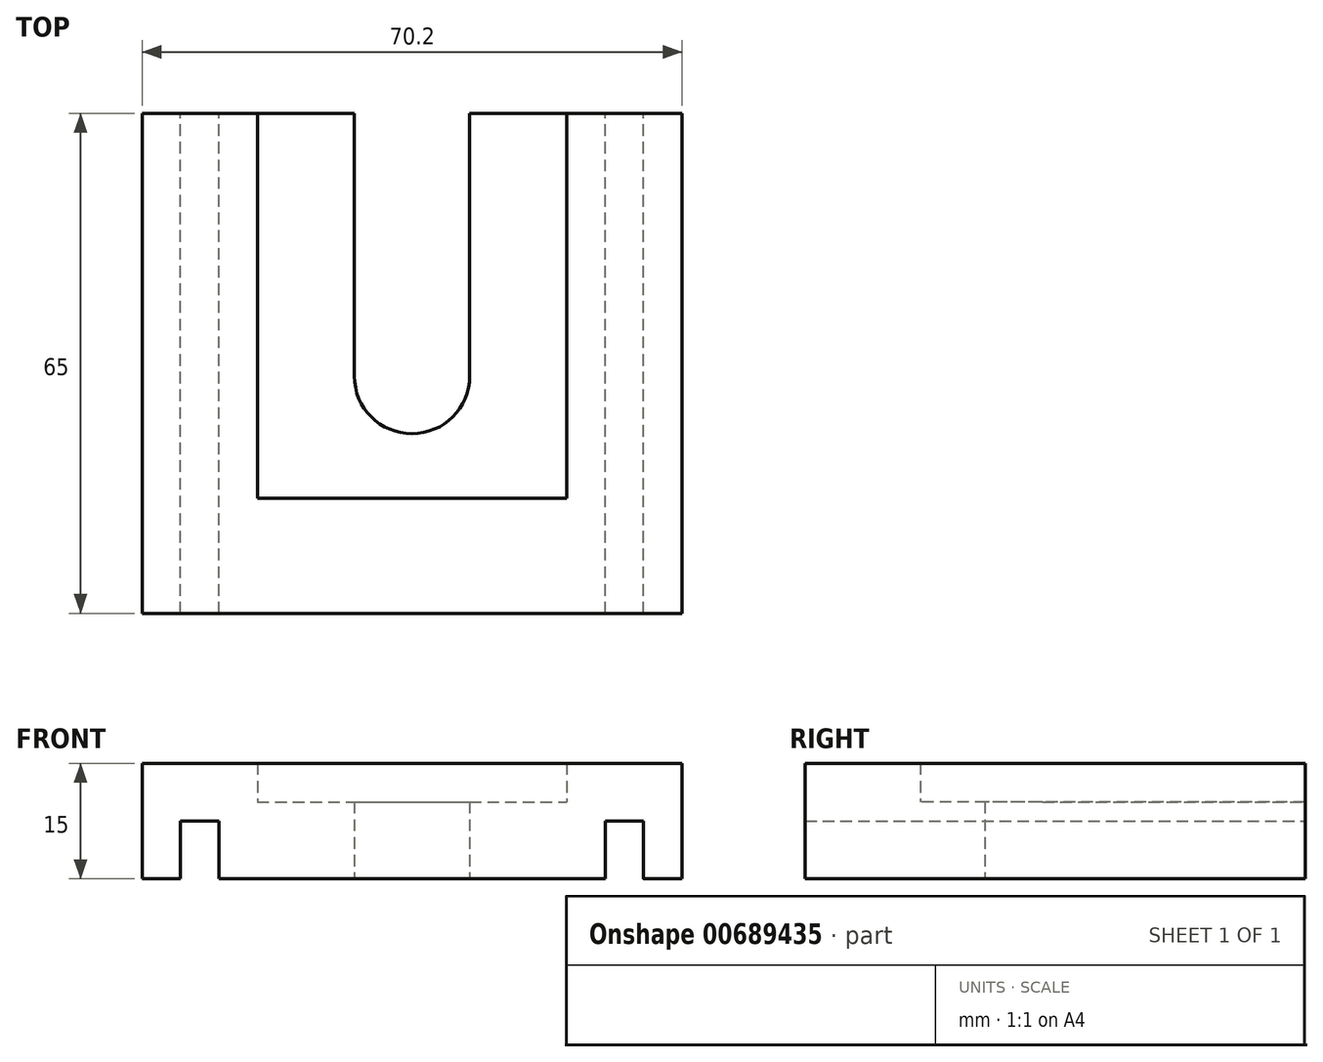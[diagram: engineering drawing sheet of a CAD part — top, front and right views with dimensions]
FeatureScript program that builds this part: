
annotation { "Feature Type Name" : "Feature", "Feature Type Description" : "" }
export const myFeature = defineFeature(function(context is Context, id is Id, definition is map)
    precondition{}
    {
        {
            var Q0;
            Q0=qCreatedBy(makeId("Top.planeOp"),FACE);
            var sketch = newSketch(context, id + "F0", { "sketchPlane" : qUnion([Q0])});
            skLineSegment(sketch, "E0.bottom", {"start": v(-49.5, 34.14) * mm, "end": v(20.7, 34.14) * mm});
            skLineSegment(sketch, "E0.top", {"start": v(-49.5, -30.86) * mm, "end": v(20.7, -30.86) * mm});
            skLineSegment(sketch, "E0.left", {"start": v(-49.5, 34.14) * mm, "end": v(-49.5, -30.86) * mm});
            skLineSegment(sketch, "E0.right", {"start": v(20.7, 34.14) * mm, "end": v(20.7, -30.86) * mm});
            skLineSegment(sketch, "E1.bottom", {"start": v(-34.5, 34.14) * mm, "end": v(5.7, 34.14) * mm});
            skLineSegment(sketch, "E1.top", {"start": v(-34.5, -15.86) * mm, "end": v(5.7, -15.86) * mm});
            skLineSegment(sketch, "E1.left", {"start": v(-34.5, 34.14) * mm, "end": v(-34.5, -15.86) * mm});
            skLineSegment(sketch, "E1.right", {"start": v(5.7, 34.14) * mm, "end": v(5.7, -15.86) * mm});
            skPoint(sketch, "E2", {"position": v(-14.4, 0) * mm});
            skCircle(sketch, "E3", {"center": v(-14.4, 0) * mm, "radius": 7.5 * mm});
            skLineSegment(sketch, "E4.bottom", {"start": v(-21.9, 0) * mm, "end": v(-6.9, 0) * mm});
            skLineSegment(sketch, "E4.top", {"start": v(-21.9, 34.14) * mm, "end": v(-6.9, 34.14) * mm});
            skLineSegment(sketch, "E4.left", {"start": v(-21.9, 0) * mm, "end": v(-21.9, 34.14) * mm});
            skLineSegment(sketch, "E4.right", {"start": v(-6.9, 0) * mm, "end": v(-6.9, 34.14) * mm});
            skSolve(sketch);
        }
        {
            var Q0;
            Q0=makeQuery(id+"F0.imprint","IMPRINT",FACE,{"disambiguationData":[TD([[makeQuery(id+"F0.imprint","IMPRINT",EDGE,{"derivedFrom":sQuery(id+"F0.wireOp",EDGE,"E0.top")}),1.0]])]});
            extrude(context, id + "F1", {"entities" : qUnion([Q0]), "depth" : 15 * mm, "offsetDistance" : 25 * mm});
        }
        {
            var Q0;
            Q0=makeQuery(id+"F0.imprint","IMPRINT",FACE,{"disambiguationData":[TD([[makeQuery(id+"F0.imprint","IMPRINT",EDGE,{"derivedFrom":sQuery(id+"F0.wireOp",EDGE,"E0.top")}),1.0]])]});
            var Q1;
            Q1=makeQuery(id+"F0.imprint","IMPRINT",FACE,{"disambiguationData":[TD([[makeQuery(id+"F0.imprint","IMPRINT",EDGE,{"derivedFrom":sQuery(id+"F0.wireOp",EDGE,"E1.top")}),1.0]])]});
            extrude(context, id + "F2", {"entities" : qUnion([Q0, Q1]), "operationType" : NewBodyOperationType.ADD, "depth" : 10 * mm, "offsetDistance" : 25 * mm});
        }
        {
            var Q0;
            Q0=makeQuery(id+"F0.imprint","IMPRINT",FACE,{"disambiguationData":[TD([[makeQuery(id+"F0.imprint","IMPRINT",EDGE,{"derivedFrom":sQuery(id+"F0.wireOp",EDGE,"E0.top")}),1.0]])]});
            var sketch = newSketch(context, id + "F3", { "sketchPlane" : qUnion([Q0])});
            skLineSegment(sketch, "E5", {"start": v(-42, -31.43) * mm, "end": v(-42, 34.7) * mm});
            skLineSegment(sketch, "E6", {"start": v(13.2, -32.09) * mm, "end": v(13.2, 34.05) * mm});
            skArc(sketch, "E7.0.startCap", {"start": v(-39.5, -31.43) * mm, "mid": v(-42, -33.93) * mm, "end": v(-44.5, -31.43) * mm});
            skArc(sketch, "E7.0.endCap", {"start": v(-44.5, 34.7) * mm, "mid": v(-42, 37.2) * mm, "end": v(-39.5, 34.7) * mm});
            skLineSegment(sketch, "E7.0.left", {"start": v(-44.5, -31.43) * mm, "end": v(-44.5, 34.7) * mm});
            skLineSegment(sketch, "E7.0.right", {"start": v(-39.5, -31.43) * mm, "end": v(-39.5, 34.7) * mm});
            skArc(sketch, "E7.1.startCap", {"start": v(15.7, -32.09) * mm, "mid": v(13.2, -34.59) * mm, "end": v(10.7, -32.09) * mm});
            skArc(sketch, "E7.1.endCap", {"start": v(10.7, 34.05) * mm, "mid": v(13.2, 36.55) * mm, "end": v(15.7, 34.05) * mm});
            skLineSegment(sketch, "E7.1.left", {"start": v(10.7, -32.09) * mm, "end": v(10.7, 34.05) * mm});
            skLineSegment(sketch, "E7.1.right", {"start": v(15.7, -32.09) * mm, "end": v(15.7, 34.05) * mm});
            skSolve(sketch);
        }
        {
            var Q0;
            {var subQ1=makeQuery(id+"F0.imprint","IMPRINT",EDGE,{"derivedFrom":sQuery(id+"F0.wireOp",EDGE,"E0.top")});var subQ6=sQuery(id+"F3.wireOp",EDGE,"E7.0.right");var subQ7=makeQuery(id+"F3.imprint","INTERSECT",VERTEX,{"derivedFrom":[subQ1,subQ6]});Q0=makeQuery(id+"F3.imprint","IMPRINT",FACE,{"disambiguationData":[TD([[makeQuery(id+"F3.imprint","IMPRINT",EDGE,{"disambiguationData":[TD([[subQ7,1.0]])],"derivedFrom":subQ1}),1.0]])]});}
            var Q1;
            {var subQ1=makeQuery(id+"F0.imprint","IMPRINT",EDGE,{"derivedFrom":sQuery(id+"F0.wireOp",EDGE,"E0.top")});var subQ6=sQuery(id+"F3.wireOp",EDGE,"E7.0.left");var subQ8=makeQuery(id+"F3.imprint","INTERSECT",VERTEX,{"derivedFrom":[subQ1,subQ6]});Q1=makeQuery(id+"F3.imprint","IMPRINT",FACE,{"disambiguationData":[TD([[makeQuery(id+"F3.imprint","IMPRINT",EDGE,{"disambiguationData":[TD([[subQ8,-1.0]])],"derivedFrom":subQ1}),1.0]])]});}
            var Q2;
            {var subQ3=makeQuery(id+"F0.imprint","IMPRINT",EDGE,{"derivedFrom":sQuery(id+"F0.wireOp",EDGE,"E0.top")});var subQ12=makeQuery(id+"F3.imprint","IMPRINT",VERTEX,{"derivedFrom":subQ3});Q2=makeQuery(id+"F3.imprint","IMPRINT",FACE,{"disambiguationData":[TD([[makeQuery(id+"F3.imprint","IMPRINT",EDGE,{"disambiguationData":[TD([[subQ12,1.0]])],"derivedFrom":subQ3}),1.0]])]});}
            extrude(context, id + "F4", {"entities" : qUnion([Q0, Q1, Q2]), "operationType" : NewBodyOperationType.REMOVE, "endBound" : BoundingType.SYMMETRIC, "oppositeDirection" : true, "depth" : 15 * mm, "offsetDistance" : 25 * mm});
        }
    });
